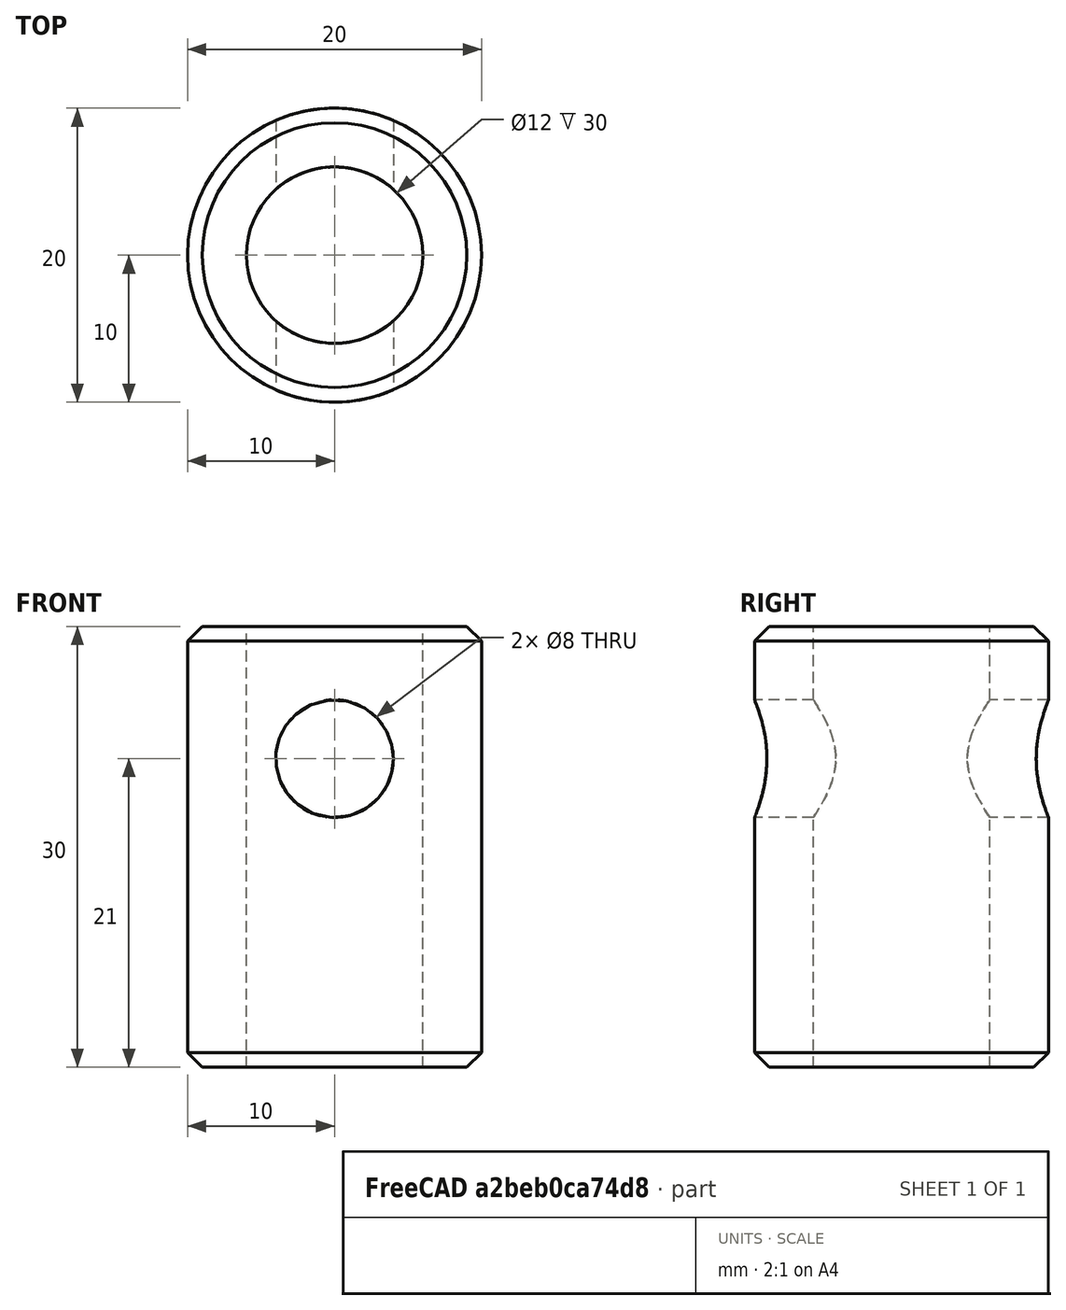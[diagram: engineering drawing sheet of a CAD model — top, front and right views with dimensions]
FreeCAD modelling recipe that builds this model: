
FCSTD DOCUMENT  (FreeCAD 0.18R4 (GitTag))
Label: ID-012-00-MRS
License: All rights reserved
LicenseURL: http://en.wikipedia.org/wiki/All_rights_reserved
objects: Part::Cylinder×3, Part::Cut×2, Part::Chamfer×2
note: 7 computed .brp shape members not serialized (recipe doc carries the construction recipe); baked Part::Feature solids carry a one-line shape summary decoded from their .brp

FEATURE [Part::Cylinder] Cylinder  label="Cilindro"
  Angle = 360
  AttacherType = Attacher::AttachEngine3D
  Height = 30
  Radius = 10
FEATURE [Part::Cylinder] Cylinder001  label="Cilindro001"
  Angle = 360
  AttacherType = Attacher::AttachEngine3D
  Height = 30
  Radius = 6
FEATURE [Part::Cut] Cut
  Base = -> Cylinder
  Tool = -> Cylinder001
FEATURE [Part::Cylinder] Cylinder002  label="Cilindro002"
  Angle = 360
  AttacherType = Attacher::AttachEngine3D
  Height = 30
  Placement = pos=(0,15,21) rot=(1,0,0;1.5708rad)
  Radius = 4
FEATURE [Part::Cut] Cut001
  Base = -> Cut
  Tool = -> Cylinder002
FEATURE [Part::Chamfer] Chamfer
  Base = -> Cut001
  Edges = 1 edges r=1: [Edge3]
FEATURE [Part::Chamfer] Chamfer001
  Base = -> Chamfer
  Edges = 1 edges r=1: [Edge3]
